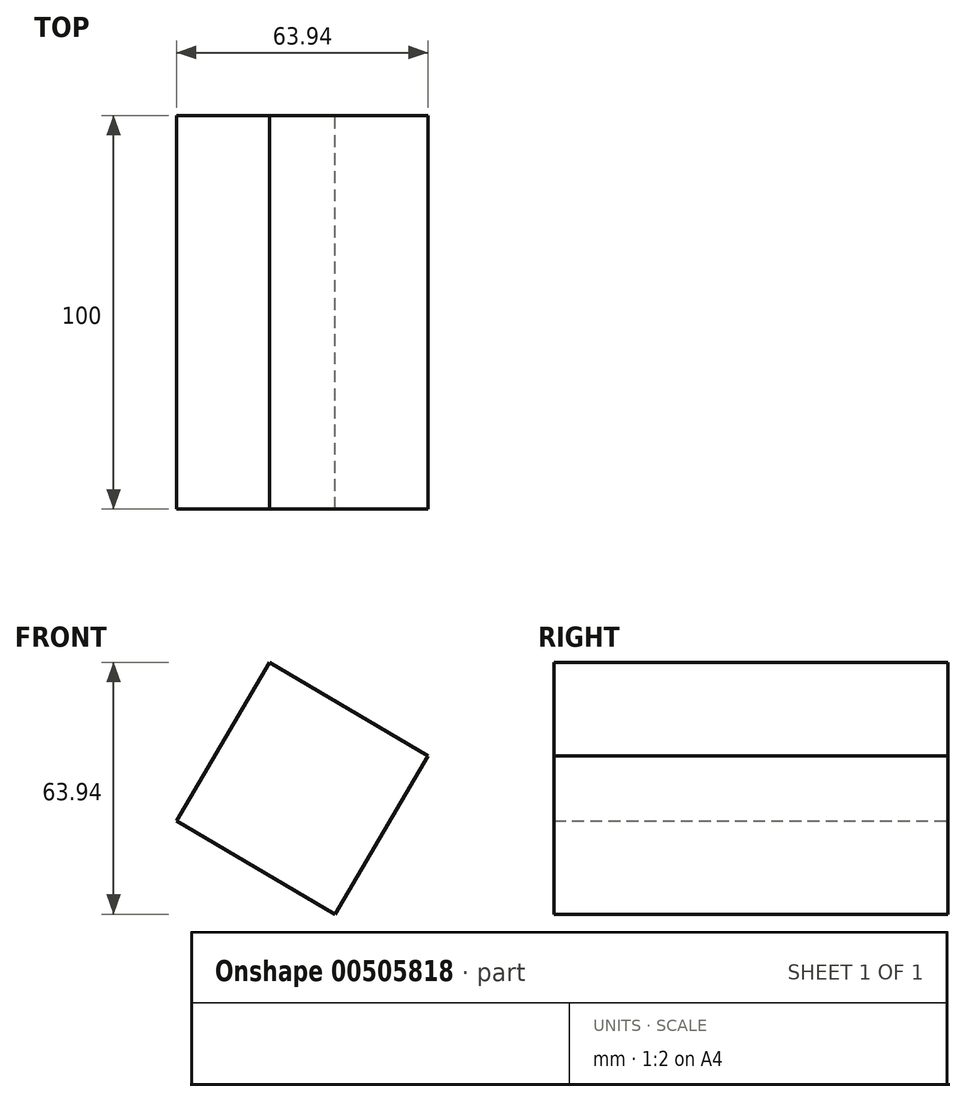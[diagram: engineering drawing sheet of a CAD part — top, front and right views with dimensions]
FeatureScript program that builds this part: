
annotation { "Feature Type Name" : "Feature", "Feature Type Description" : "" }
export const myFeature = defineFeature(function(context is Context, id is Id, definition is map)
    precondition{}
    {
        {
            var Q0;
            Q0=qCreatedBy(makeId("Front.planeOp"),FACE);
            var sketch = newSketch(context, id + "F0", { "sketchPlane" : qUnion([Q0])});
            skCircle(sketch, "E0.cCircle", {"center": v(0, 0) * mm, "radius": 23.36 * mm, "construction": true});
            skLineSegment(sketch, "E0.0", {"start": v(-31.97, -8.29) * mm, "end": v(-8.29, 31.97) * mm});
            skLineSegment(sketch, "E0.1", {"start": v(-8.29, 31.97) * mm, "end": v(31.97, 8.29) * mm});
            skLineSegment(sketch, "E0.2", {"start": v(31.97, 8.29) * mm, "end": v(8.29, -31.97) * mm});
            skLineSegment(sketch, "E0.3", {"start": v(8.29, -31.97) * mm, "end": v(-31.97, -8.29) * mm});
            skPoint(sketch, "E0.0.midPoint", {"position": v(-20.13, 11.84) * mm});
            skSolve(sketch);
        }
        {
            var Q0;
            Q0 = qSketchRegion(id + "F0", true);
            extrude(context, id + "F1", {"entities" : qUnion([Q0]), "endBound" : BoundingType.SYMMETRIC, "depth" : 100 * mm});
        }
    });
